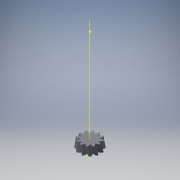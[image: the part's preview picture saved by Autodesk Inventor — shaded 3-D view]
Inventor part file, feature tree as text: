
AUTODESK INVENTOR PART (.ipt)
format: ipt  version: 2016 (Build 200138000, 138)  size: 501,248 bytes
history: native  units: mm
features: other x24, loft x2, pattern_circular x2, sketch x1
ambient origin geometry x6: Origin, XZ Plane, X Axis, Y Axis, Z Axis, Center Point
bodies: Solid1 (feature_tree)
feature tree (29):
  other  "Top Point"
  other  "Mesh Plane2"
  other  "Teeth Body"
  other  "Start Point"
  other  "Tooth Plane"
  other  "Start Sketch"
  other  "End Point"
  other  "3D Sketch Right"
  other  "End Plane Right"
  loft  "Loft Right"
  pattern_circular  "Circular Pattern Right"  [2 undecoded]
  other  "3D Sketch Left"
  other  "End Plane Left"
  loft  "Loft Left"
  pattern_circular  "Circular Pattern Left"  [2 undecoded]
  other  "Fix Body"
  other  "Mesh Plane"
  other  "Top Plane"
  other  "Teeth Body Sketch"
  other  "End Plane"
  other  "End Sketch"
  other  "Helical Curve Left"
  other  "End Sketch Left"
  other  "Body Sketch"
  sketch  "Sketch6"  dims[d0=30.48mm d1=24.411898mm d2=35.170288mm d3=12.7mm d4=158.524866mm d5=90.0deg d7=7.848201mm d8=8.304714mm d9=10.52094mm d11=12.970196mm d12=7.21777mm d15=7.637612mm d16=9.675812mm d17=0.0mm d18=90.0deg d19=0.0mm d20=90.0deg d21=120.0mm d22=360.0deg d26=341.565783mm d27=12.91084mm d28=30.48mm d29=-0.957067mm d30=7.21777mm d31=7.637612mm d32=9.675812mm d35=0.0mm d37=0.0mm d39=0.0mm d40=90.0deg d41=120.0mm d42=360.0deg d46=90.0deg d47=90.0deg d48=0.0mm d49=0.0mm d50=90.0deg d51=15.0deg d52=0.0mm d53=0.0mm d54=0.0mm d56=16.110741mm d57=19.287168mm d58=11.613594mm d59=17.737866mm d60=10.680696mm d61=17.737866mm d62=10.680696mm d63=90.0deg d64=90.0deg d65=341.565783mm d66=31.5mm d67=30.48mm d68=-0.957067mm d69=12.91084mm d70=7.637612mm d71=9.675812mm d72=7.21777mm d73=10.680696mm d74=17.737866mm d75=0.0mm d76=90.0deg d77=0.0mm d78=90.0deg d79=0.0mm d80=90.0deg d81=120.0mm d82=360.0deg d84=10.0mm d85=20.0mm d86=20.0mm d87=10.0mm d88=0.0mm d89=0.0mm]
  other  "Srf1"
  other  "Helical Curve Right"
  other  "End Sketch Right"
  other  "Pitch Diameter"
note: 4 required parameter values undecoded (feature->parameter linkage not recoverable at this tier; creation-order binding heuristic only, values carry confidence <= 0.55)
